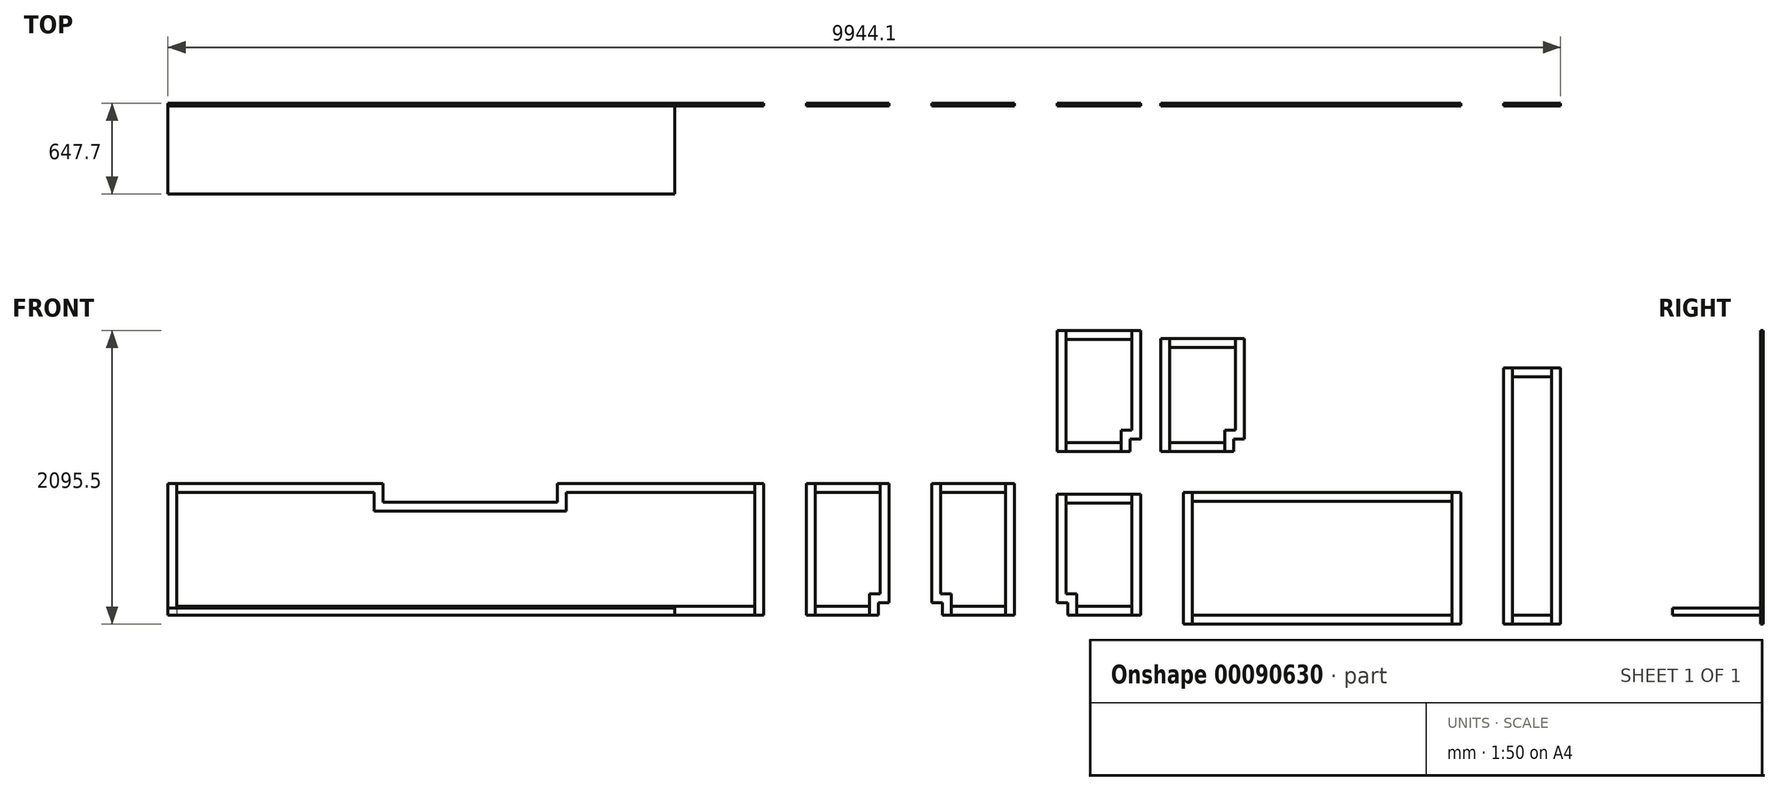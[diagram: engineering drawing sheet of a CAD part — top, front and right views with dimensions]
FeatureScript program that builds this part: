
annotation { "Feature Type Name" : "Feature", "Feature Type Description" : "" }
export const myFeature = defineFeature(function(context is Context, id is Id, definition is map)
    precondition{}
    {
        {
            var Q0;
            Q0=qCreatedBy(makeId("Top.planeOp"),FACE);
            var sketch = newSketch(context, id + "F0", { "sketchPlane" : qUnion([Q0])});
            skLineSegment(sketch, "E0.bottom", {"start": v(0, 0) * mm, "end": v(3619.5, 0) * mm});
            skLineSegment(sketch, "E0.top", {"start": v(0, -647.7) * mm, "end": v(3619.5, -647.7) * mm});
            skLineSegment(sketch, "E0.left", {"start": v(0, 0) * mm, "end": v(0, -647.7) * mm});
            skLineSegment(sketch, "E0.right", {"start": v(3619.5, 0) * mm, "end": v(3619.5, -647.7) * mm});
            skSolve(sketch);
        }
        {
            var Q0;
            Q0 = qSketchRegion(id + "F0", true);
            extrude(context, id + "F1", {"entities" : qUnion([Q0]), "depth" : 50.8 * mm});
        }
        {
            var Q0;
            Q0=qCreatedBy(makeId("Front.planeOp"),FACE);
            var sketch = newSketch(context, id + "F2", { "sketchPlane" : qUnion([Q0])});
            skLineSegment(sketch, "E1.bottom", {"start": v(0, 0) * mm, "end": v(4254.5, 0) * mm});
            skLineSegment(sketch, "E1.top", {"start": v(0, 939.8) * mm, "end": v(4254.5, 939.8) * mm});
            skLineSegment(sketch, "E1.left", {"start": v(0, 0) * mm, "end": v(0, 939.8) * mm});
            skLineSegment(sketch, "E1.right", {"start": v(4254.5, 0) * mm, "end": v(4254.5, 939.8) * mm});
            skLineSegment(sketch, "E2", {"start": v(1536.7, 939.8) * mm, "end": v(1536.7, 806.45) * mm});
            skLineSegment(sketch, "E3", {"start": v(1536.7, 806.45) * mm, "end": v(2781.3, 806.45) * mm});
            skLineSegment(sketch, "E4", {"start": v(2781.3, 806.45) * mm, "end": v(2781.3, 939.8) * mm});
            skLineSegment(sketch, "E5", {"start": v(63.5, 939.8) * mm, "end": v(63.5, 0) * mm});
            skLineSegment(sketch, "E6", {"start": v(4191, 939.8) * mm, "end": v(4191, 0) * mm});
            skLineSegment(sketch, "E7", {"start": v(63.5, 876.3) * mm, "end": v(1473.2, 876.3) * mm});
            skLineSegment(sketch, "E8", {"start": v(1473.2, 876.3) * mm, "end": v(1473.2, 742.95) * mm});
            skLineSegment(sketch, "E9", {"start": v(1473.2, 742.95) * mm, "end": v(2844.8, 742.95) * mm});
            skLineSegment(sketch, "E10", {"start": v(2844.8, 742.95) * mm, "end": v(2844.8, 876.3) * mm});
            skLineSegment(sketch, "E11", {"start": v(2844.8, 876.3) * mm, "end": v(4191, 876.3) * mm});
            skLineSegment(sketch, "E12", {"start": v(63.5, 63.5) * mm, "end": v(4191, 63.5) * mm});
            skLineSegment(sketch, "E13", {"start": v(4191, 469.9) * mm, "end": v(4254.5, 469.9) * mm, "construction": true});
            skLineSegment(sketch, "E14", {"start": v(3517.9, 876.3) * mm, "end": v(3517.9, 939.8) * mm, "construction": true});
            skLineSegment(sketch, "E15", {"start": v(2844.8, 876.3) * mm, "end": v(2781.3, 876.3) * mm, "construction": true});
            skLineSegment(sketch, "E16", {"start": v(2144.3, 806.45) * mm, "end": v(2144.3, 742.95) * mm, "construction": true});
            skLineSegment(sketch, "E17", {"start": v(1473.2, 824.4) * mm, "end": v(1536.7, 824.4) * mm, "construction": true});
            skLineSegment(sketch, "E18", {"start": v(768.35, 876.3) * mm, "end": v(768.35, 939.8) * mm, "construction": true});
            skLineSegment(sketch, "E19", {"start": v(63.5, 469.9) * mm, "end": v(0, 469.9) * mm, "construction": true});
            skLineSegment(sketch, "E20", {"start": v(1679.38, 63.5) * mm, "end": v(1679.38, 0) * mm, "construction": true});
            skSolve(sketch);
        }
        {
            var Q0;
            {var subQ4=sQuery(id+"F2.wireOp",EDGE,"E1.left");Q0=makeQuery(id+"F2.imprint","IMPRINT",FACE,{"disambiguationData":[TD([[makeQuery(id+"F2.imprint","IMPRINT",EDGE,{"derivedFrom":subQ4}),-1.0]])]});}
            var Q1;
            {var subQ0=sQuery(id+"F2.wireOp",EDGE,"E1.right");Q1=makeQuery(id+"F2.imprint","IMPRINT",FACE,{"disambiguationData":[TD([[makeQuery(id+"F2.imprint","IMPRINT",EDGE,{"derivedFrom":subQ0}),1.0]])]});}
            extrude(context, id + "F3", {"entities" : qUnion([Q0, Q1]), "depth" : 19.05 * mm});
        }
        {
            var Q0;
            {var subQ8=sQuery(id+"F2.wireOp",EDGE,"E2");Q0=makeQuery(id+"F2.imprint","IMPRINT",FACE,{"disambiguationData":[TD([[makeQuery(id+"F2.imprint","IMPRINT",EDGE,{"derivedFrom":subQ8}),-1.0]])]});}
            var Q1;
            {var subQ5=sQuery(id+"F2.wireOp",EDGE,"E12");Q1=makeQuery(id+"F2.imprint","IMPRINT",FACE,{"disambiguationData":[TD([[makeQuery(id+"F2.imprint","IMPRINT",EDGE,{"derivedFrom":subQ5}),-1.0]])]});}
            extrude(context, id + "F4", {"entities" : qUnion([Q0, Q1]), "depth" : 19.05 * mm});
        }
        {
            var Q0;
            {var subQ0=sQuery(id+"F2.wireOp",EDGE,"E7");Q0=makeQuery(id+"F2.imprint","IMPRINT",FACE,{"disambiguationData":[TD([[makeQuery(id+"F2.imprint","IMPRINT",EDGE,{"derivedFrom":subQ0}),-1.0]])]});}
            extrude(context, id + "F5", {"entities" : qUnion([Q0]), "depth" : 9.52 * mm});
        }
        {
            var Q0;
            Q0=qCreatedBy(makeId("Front.planeOp"),FACE);
            var sketch = newSketch(context, id + "F6", { "sketchPlane" : qUnion([Q0])});
            skLineSegment(sketch, "E21.bottom", {"start": v(4559.3, 0) * mm, "end": v(5149.85, 0) * mm});
            skLineSegment(sketch, "E21.top", {"start": v(4559.3, 939.8) * mm, "end": v(5149.85, 939.8) * mm});
            skLineSegment(sketch, "E21.left", {"start": v(4559.3, 0) * mm, "end": v(4559.3, 939.8) * mm});
            skLineSegment(sketch, "E21.right", {"start": v(5149.85, 0) * mm, "end": v(5149.85, 939.8) * mm});
            skLineSegment(sketch, "E22", {"start": v(5073.65, 0) * mm, "end": v(5073.65, 88.9) * mm});
            skLineSegment(sketch, "E23", {"start": v(5073.65, 88.9) * mm, "end": v(5149.85, 88.9) * mm});
            skLineSegment(sketch, "E24", {"start": v(4622.8, 939.8) * mm, "end": v(4622.8, 0) * mm});
            skLineSegment(sketch, "E25", {"start": v(5086.35, 939.8) * mm, "end": v(5086.35, 152.4) * mm});
            skLineSegment(sketch, "E26", {"start": v(5086.35, 152.4) * mm, "end": v(5010.15, 152.4) * mm});
            skLineSegment(sketch, "E27", {"start": v(5010.15, 152.4) * mm, "end": v(5010.15, 0) * mm});
            skLineSegment(sketch, "E28", {"start": v(4622.8, 63.5) * mm, "end": v(5010.15, 63.5) * mm});
            skLineSegment(sketch, "E29", {"start": v(4622.8, 876.3) * mm, "end": v(5086.35, 876.3) * mm});
            skLineSegment(sketch, "E30", {"start": v(4854.57, 939.8) * mm, "end": v(4854.57, 876.3) * mm, "construction": true});
            skLineSegment(sketch, "E31", {"start": v(5149.85, 469.9) * mm, "end": v(5086.35, 469.9) * mm, "construction": true});
            skLineSegment(sketch, "E32", {"start": v(4559.3, 469.9) * mm, "end": v(4622.8, 469.9) * mm, "construction": true});
            skLineSegment(sketch, "E33", {"start": v(4816.48, 63.5) * mm, "end": v(4816.48, 0) * mm, "construction": true});
            skLineSegment(sketch, "E34", {"start": v(5073.65, 44.45) * mm, "end": v(5010.15, 44.45) * mm, "construction": true});
            skLineSegment(sketch, "E35", {"start": v(5111.75, 88.9) * mm, "end": v(5111.75, 152.4) * mm, "construction": true});
            skLineSegment(sketch, "E36", {"start": v(5302.25, 0) * mm, "end": v(5302.25, 939.8) * mm, "construction": true});
            skLineSegment(sketch, "E37.MirrorCS", {"start": v(6045.2, 469.9) * mm, "end": v(5981.7, 469.9) * mm, "construction": true});
            skLineSegment(sketch, "E38.MirrorCS", {"start": v(5530.85, 44.45) * mm, "end": v(5594.35, 44.45) * mm, "construction": true});
            skLineSegment(sketch, "E39.MirrorCS", {"start": v(5749.93, 939.8) * mm, "end": v(5749.93, 876.3) * mm, "construction": true});
            skLineSegment(sketch, "E40.MirrorCS", {"start": v(5788.02, 63.5) * mm, "end": v(5788.02, 0) * mm, "construction": true});
            skLineSegment(sketch, "E41.MirrorCS", {"start": v(5454.65, 469.9) * mm, "end": v(5518.15, 469.9) * mm, "construction": true});
            skLineSegment(sketch, "E42.MirrorCS", {"start": v(5492.75, 88.9) * mm, "end": v(5492.75, 152.4) * mm, "construction": true});
            skLineSegment(sketch, "E43.MirrorCS", {"start": v(5530.85, 0) * mm, "end": v(5530.85, 88.9) * mm});
            skLineSegment(sketch, "E44.MirrorCS", {"start": v(5530.85, 88.9) * mm, "end": v(5454.65, 88.9) * mm});
            skLineSegment(sketch, "E45.MirrorCS", {"start": v(5594.35, 152.4) * mm, "end": v(5594.35, 0) * mm});
            skLineSegment(sketch, "E46.MirrorCS", {"start": v(5981.7, 63.5) * mm, "end": v(5594.35, 63.5) * mm});
            skLineSegment(sketch, "E47.MirrorCS", {"start": v(5518.15, 152.4) * mm, "end": v(5594.35, 152.4) * mm});
            skLineSegment(sketch, "E48.MirrorCS", {"start": v(5518.15, 939.8) * mm, "end": v(5518.15, 152.4) * mm});
            skLineSegment(sketch, "E49.MirrorCS", {"start": v(5981.7, 939.8) * mm, "end": v(5981.7, 0) * mm});
            skLineSegment(sketch, "E50.MirrorCS", {"start": v(6045.2, 0) * mm, "end": v(5454.65, 0) * mm});
            skLineSegment(sketch, "E51.MirrorCS", {"start": v(6045.2, 939.8) * mm, "end": v(5454.65, 939.8) * mm});
            skLineSegment(sketch, "E52.MirrorCS", {"start": v(6045.2, 0) * mm, "end": v(6045.2, 939.8) * mm});
            skLineSegment(sketch, "E53.MirrorCS", {"start": v(5454.65, 0) * mm, "end": v(5454.65, 939.8) * mm});
            skLineSegment(sketch, "E54.MirrorCS", {"start": v(5981.7, 876.3) * mm, "end": v(5518.15, 876.3) * mm});
            skLineSegment(sketch, "E55.bottom", {"start": v(6946.9, 0) * mm, "end": v(6350, 0) * mm});
            skLineSegment(sketch, "E55.top", {"start": v(6946.9, 863.6) * mm, "end": v(6350, 863.6) * mm});
            skLineSegment(sketch, "E55.left", {"start": v(6946.9, 0) * mm, "end": v(6946.9, 863.6) * mm});
            skLineSegment(sketch, "E55.right", {"start": v(6350, 0) * mm, "end": v(6350, 863.6) * mm});
            skLineSegment(sketch, "E56", {"start": v(6350, 88.9) * mm, "end": v(6426.2, 88.9) * mm});
            skLineSegment(sketch, "E57", {"start": v(6426.2, 88.9) * mm, "end": v(6426.2, 0) * mm});
            skLineSegment(sketch, "E58", {"start": v(6413.5, 863.6) * mm, "end": v(6413.5, 152.4) * mm});
            skLineSegment(sketch, "E59", {"start": v(6413.5, 152.4) * mm, "end": v(6489.7, 152.4) * mm});
            skLineSegment(sketch, "E60", {"start": v(6489.7, 152.4) * mm, "end": v(6489.7, 0) * mm});
            skLineSegment(sketch, "E61", {"start": v(6883.4, 0) * mm, "end": v(6883.4, 863.6) * mm});
            skLineSegment(sketch, "E62", {"start": v(6883.4, 800.1) * mm, "end": v(6413.5, 800.1) * mm});
            skLineSegment(sketch, "E63", {"start": v(6489.7, 63.5) * mm, "end": v(6883.4, 63.5) * mm});
            skLineSegment(sketch, "E64", {"start": v(6946.9, 431.8) * mm, "end": v(6883.4, 431.8) * mm, "construction": true});
            skLineSegment(sketch, "E65", {"start": v(6648.45, 863.6) * mm, "end": v(6648.45, 800.1) * mm, "construction": true});
            skLineSegment(sketch, "E66", {"start": v(6350, 431.8) * mm, "end": v(6413.5, 431.8) * mm, "construction": true});
            skLineSegment(sketch, "E67", {"start": v(6686.55, 63.5) * mm, "end": v(6686.55, 0) * mm, "construction": true});
            skLineSegment(sketch, "E68", {"start": v(6426.2, 44.45) * mm, "end": v(6489.7, 44.45) * mm, "construction": true});
            skLineSegment(sketch, "E69", {"start": v(6388.1, 88.9) * mm, "end": v(6388.1, 152.4) * mm, "construction": true});
            skLineSegment(sketch, "E70.bottom", {"start": v(7251.7, 876.3) * mm, "end": v(9232.9, 876.3) * mm});
            skLineSegment(sketch, "E70.top", {"start": v(7251.7, -63.5) * mm, "end": v(9232.9, -63.5) * mm});
            skLineSegment(sketch, "E70.left", {"start": v(7251.7, 876.3) * mm, "end": v(7251.7, -63.5) * mm});
            skLineSegment(sketch, "E70.right", {"start": v(9232.9, 876.3) * mm, "end": v(9232.9, -63.5) * mm});
            skLineSegment(sketch, "E71", {"start": v(7315.2, 876.3) * mm, "end": v(7315.2, -63.5) * mm});
            skLineSegment(sketch, "E72", {"start": v(9169.4, 876.3) * mm, "end": v(9169.4, -63.5) * mm});
            skLineSegment(sketch, "E73", {"start": v(7315.2, 812.8) * mm, "end": v(9169.4, 812.8) * mm});
            skLineSegment(sketch, "E74", {"start": v(7315.2, 0) * mm, "end": v(9169.4, 0) * mm});
            skLineSegment(sketch, "E75", {"start": v(9232.9, 406.4) * mm, "end": v(9169.4, 406.4) * mm, "construction": true});
            skLineSegment(sketch, "E76", {"start": v(8261.12, 876.3) * mm, "end": v(8261.12, 812.8) * mm, "construction": true});
            skLineSegment(sketch, "E77", {"start": v(7251.7, 406.4) * mm, "end": v(7315.2, 406.4) * mm, "construction": true});
            skLineSegment(sketch, "E78", {"start": v(8242.3, 0) * mm, "end": v(8242.3, -63.5) * mm, "construction": true});
            skLineSegment(sketch, "E79.bottom", {"start": v(9537.7, -63.5) * mm, "end": v(9944.1, -63.5) * mm});
            skLineSegment(sketch, "E79.top", {"start": v(9537.7, 1765.3) * mm, "end": v(9944.1, 1765.3) * mm});
            skLineSegment(sketch, "E79.left", {"start": v(9537.7, -63.5) * mm, "end": v(9537.7, 1765.3) * mm});
            skLineSegment(sketch, "E79.right", {"start": v(9944.1, -63.5) * mm, "end": v(9944.1, 1765.3) * mm});
            skLineSegment(sketch, "E80.bottom", {"start": v(9880.6, 0) * mm, "end": v(9601.2, 0) * mm});
            skLineSegment(sketch, "E80.top", {"start": v(9880.6, 1701.8) * mm, "end": v(9601.2, 1701.8) * mm});
            skLineSegment(sketch, "E80.left", {"start": v(9880.6, 0) * mm, "end": v(9880.6, 1701.8) * mm});
            skLineSegment(sketch, "E80.right", {"start": v(9601.2, 0) * mm, "end": v(9601.2, 1701.8) * mm});
            skLineSegment(sketch, "E81", {"start": v(9740.9, 1765.3) * mm, "end": v(9740.9, 1701.8) * mm, "construction": true});
            skPoint(sketch, "E81.endSnap0", {"position": v(9740.9, 1701.8) * mm});
            skLineSegment(sketch, "E82", {"start": v(9944.1, 850.9) * mm, "end": v(9880.6, 850.9) * mm, "construction": true});
            skLineSegment(sketch, "E83", {"start": v(9537.7, 850.9) * mm, "end": v(9601.2, 850.9) * mm, "construction": true});
            skLineSegment(sketch, "E84", {"start": v(9740.9, -63.5) * mm, "end": v(9740.9, 0) * mm, "construction": true});
            skLineSegment(sketch, "E85", {"start": v(9601.2, 1701.8) * mm, "end": v(9601.2, 1765.3) * mm});
            skLineSegment(sketch, "E86", {"start": v(9880.6, 1701.8) * mm, "end": v(9880.6, 1765.3) * mm});
            skLineSegment(sketch, "E87", {"start": v(9601.2, 0) * mm, "end": v(9601.2, -63.5) * mm});
            skLineSegment(sketch, "E88", {"start": v(9880.6, 0) * mm, "end": v(9880.6, -63.5) * mm});
            skLineSegment(sketch, "E89.bottom", {"start": v(6350, 2032) * mm, "end": v(6946.9, 2032) * mm});
            skLineSegment(sketch, "E89.top", {"start": v(6350, 1168.4) * mm, "end": v(6946.9, 1168.4) * mm});
            skLineSegment(sketch, "E89.left", {"start": v(6350, 2032) * mm, "end": v(6350, 1168.4) * mm});
            skLineSegment(sketch, "E89.right", {"start": v(6946.9, 2032) * mm, "end": v(6946.9, 1168.4) * mm});
            skLineSegment(sketch, "E90", {"start": v(6883.4, 2032) * mm, "end": v(6883.4, 1320.8) * mm});
            skLineSegment(sketch, "E91", {"start": v(6883.4, 1320.8) * mm, "end": v(6807.2, 1320.8) * mm});
            skLineSegment(sketch, "E92", {"start": v(6807.2, 1320.8) * mm, "end": v(6807.2, 1168.4) * mm});
            skLineSegment(sketch, "E93", {"start": v(6413.5, 2032) * mm, "end": v(6413.5, 1168.4) * mm});
            skLineSegment(sketch, "E94", {"start": v(6413.5, 1968.5) * mm, "end": v(6883.4, 1968.5) * mm});
            skLineSegment(sketch, "E95", {"start": v(6807.2, 1231.9) * mm, "end": v(6413.5, 1231.9) * mm});
            skLineSegment(sketch, "E96", {"start": v(6610.35, 1231.9) * mm, "end": v(6610.35, 1168.4) * mm, "construction": true});
            skLineSegment(sketch, "E97", {"start": v(6413.5, 1600.2) * mm, "end": v(6350, 1600.2) * mm, "construction": true});
            skLineSegment(sketch, "E98", {"start": v(6883.4, 1676.4) * mm, "end": v(6946.9, 1676.4) * mm, "construction": true});
            skLineSegment(sketch, "E99", {"start": v(6648.45, 1968.5) * mm, "end": v(6648.45, 2032) * mm, "construction": true});
            skLineSegment(sketch, "E100", {"start": v(6870.7, 1168.4) * mm, "end": v(6870.7, 1257.3) * mm});
            skLineSegment(sketch, "E101", {"start": v(6870.7, 1257.3) * mm, "end": v(6946.9, 1257.3) * mm});
            skLineSegment(sketch, "E102.bottom", {"start": v(7089.73, 1974.85) * mm, "end": v(7686.63, 1974.85) * mm});
            skLineSegment(sketch, "E102.top", {"start": v(7089.73, 1168.4) * mm, "end": v(7686.63, 1168.4) * mm});
            skLineSegment(sketch, "E102.left", {"start": v(7089.73, 1974.85) * mm, "end": v(7089.73, 1168.4) * mm});
            skLineSegment(sketch, "E102.right", {"start": v(7686.63, 1974.85) * mm, "end": v(7686.63, 1168.4) * mm});
            skLineSegment(sketch, "E103", {"start": v(7623.13, 1974.85) * mm, "end": v(7623.13, 1320.8) * mm});
            skLineSegment(sketch, "E104", {"start": v(7623.13, 1320.8) * mm, "end": v(7546.93, 1320.8) * mm});
            skLineSegment(sketch, "E105", {"start": v(7546.93, 1320.8) * mm, "end": v(7546.93, 1168.4) * mm});
            skLineSegment(sketch, "E106", {"start": v(7153.23, 1974.85) * mm, "end": v(7153.23, 1168.4) * mm});
            skLineSegment(sketch, "E107", {"start": v(7153.23, 1911.35) * mm, "end": v(7623.13, 1911.35) * mm});
            skLineSegment(sketch, "E108", {"start": v(7546.93, 1231.9) * mm, "end": v(7153.23, 1231.9) * mm});
            skLineSegment(sketch, "E109", {"start": v(7350.08, 1231.9) * mm, "end": v(7350.08, 1168.4) * mm, "construction": true});
            skLineSegment(sketch, "E110", {"start": v(7153.23, 1571.62) * mm, "end": v(7089.73, 1571.62) * mm, "construction": true});
            skLineSegment(sketch, "E111", {"start": v(7623.13, 1647.83) * mm, "end": v(7686.63, 1647.83) * mm, "construction": true});
            skLineSegment(sketch, "E112", {"start": v(7388.18, 1911.35) * mm, "end": v(7388.18, 1974.85) * mm, "construction": true});
            skLineSegment(sketch, "E113", {"start": v(7610.43, 1168.4) * mm, "end": v(7610.43, 1257.3) * mm});
            skLineSegment(sketch, "E114", {"start": v(7610.43, 1257.3) * mm, "end": v(7686.63, 1257.3) * mm});
            skSolve(sketch);
        }
        {
            var Q0;
            {var subQ0=sQuery(id+"F6.wireOp",EDGE,"E21.left");Q0=makeQuery(id+"F6.imprint","IMPRINT",FACE,{"disambiguationData":[TD([[makeQuery(id+"F6.imprint","IMPRINT",EDGE,{"derivedFrom":subQ0}),-1.0]])]});}
            var Q1;
            {var subQ4=sQuery(id+"F6.wireOp",EDGE,"E22");Q1=makeQuery(id+"F6.imprint","IMPRINT",FACE,{"disambiguationData":[TD([[makeQuery(id+"F6.imprint","IMPRINT",EDGE,{"derivedFrom":subQ4}),1.0]])]});}
            var Q2;
            {var subQ4=sQuery(id+"F6.wireOp",EDGE,"E43.MirrorCS");Q2=makeQuery(id+"F6.imprint","IMPRINT",FACE,{"disambiguationData":[TD([[makeQuery(id+"F6.imprint","IMPRINT",EDGE,{"derivedFrom":subQ4}),-1.0]])]});}
            var Q3;
            {var subQ3=sQuery(id+"F6.wireOp",EDGE,"E52.MirrorCS");Q3=makeQuery(id+"F6.imprint","IMPRINT",FACE,{"disambiguationData":[TD([[makeQuery(id+"F6.imprint","IMPRINT",EDGE,{"derivedFrom":subQ3}),1.0]])]});}
            var Q4;
            {var subQ3=sQuery(id+"F6.wireOp",EDGE,"E56");Q4=makeQuery(id+"F6.imprint","IMPRINT",FACE,{"disambiguationData":[TD([[makeQuery(id+"F6.imprint","IMPRINT",EDGE,{"derivedFrom":subQ3}),1.0]])]});}
            var Q5;
            {var subQ4=sQuery(id+"F6.wireOp",EDGE,"E55.left");Q5=makeQuery(id+"F6.imprint","IMPRINT",FACE,{"disambiguationData":[TD([[makeQuery(id+"F6.imprint","IMPRINT",EDGE,{"derivedFrom":subQ4}),1.0]])]});}
            var Q6;
            {var subQ0=sQuery(id+"F6.wireOp",EDGE,"E70.left");Q6=makeQuery(id+"F6.imprint","IMPRINT",FACE,{"disambiguationData":[TD([[makeQuery(id+"F6.imprint","IMPRINT",EDGE,{"derivedFrom":subQ0}),1.0]])]});}
            var Q7;
            {var subQ4=sQuery(id+"F6.wireOp",EDGE,"E70.right");Q7=makeQuery(id+"F6.imprint","IMPRINT",FACE,{"disambiguationData":[TD([[makeQuery(id+"F6.imprint","IMPRINT",EDGE,{"derivedFrom":subQ4}),-1.0]])]});}
            extrude(context, id + "F7", {"entities" : qUnion([Q0, Q1, Q2, Q3, Q4, Q5, Q6, Q7]), "depth" : 19.05 * mm});
        }
        {
            var Q0;
            {var subQ5=sQuery(id+"F6.wireOp",EDGE,"E29");Q0=makeQuery(id+"F6.imprint","IMPRINT",FACE,{"disambiguationData":[TD([[makeQuery(id+"F6.imprint","IMPRINT",EDGE,{"derivedFrom":subQ5}),1.0]])]});}
            var Q1;
            {var subQ5=sQuery(id+"F6.wireOp",EDGE,"E28");Q1=makeQuery(id+"F6.imprint","IMPRINT",FACE,{"disambiguationData":[TD([[makeQuery(id+"F6.imprint","IMPRINT",EDGE,{"derivedFrom":subQ5}),-1.0]])]});}
            var Q2;
            {var subQ3=sQuery(id+"F6.wireOp",EDGE,"E54.MirrorCS");Q2=makeQuery(id+"F6.imprint","IMPRINT",FACE,{"disambiguationData":[TD([[makeQuery(id+"F6.imprint","IMPRINT",EDGE,{"derivedFrom":subQ3}),-1.0]])]});}
            var Q3;
            {var subQ3=sQuery(id+"F6.wireOp",EDGE,"E46.MirrorCS");Q3=makeQuery(id+"F6.imprint","IMPRINT",FACE,{"disambiguationData":[TD([[makeQuery(id+"F6.imprint","IMPRINT",EDGE,{"derivedFrom":subQ3}),1.0]])]});}
            var Q4;
            {var subQ5=sQuery(id+"F6.wireOp",EDGE,"E62");Q4=makeQuery(id+"F6.imprint","IMPRINT",FACE,{"disambiguationData":[TD([[makeQuery(id+"F6.imprint","IMPRINT",EDGE,{"derivedFrom":subQ5}),-1.0]])]});}
            var Q5;
            {var subQ5=sQuery(id+"F6.wireOp",EDGE,"E63");Q5=makeQuery(id+"F6.imprint","IMPRINT",FACE,{"disambiguationData":[TD([[makeQuery(id+"F6.imprint","IMPRINT",EDGE,{"derivedFrom":subQ5}),-1.0]])]});}
            var Q6;
            {var subQ5=sQuery(id+"F6.wireOp",EDGE,"E73");Q6=makeQuery(id+"F6.imprint","IMPRINT",FACE,{"disambiguationData":[TD([[makeQuery(id+"F6.imprint","IMPRINT",EDGE,{"derivedFrom":subQ5}),1.0]])]});}
            var Q7;
            {var subQ5=sQuery(id+"F6.wireOp",EDGE,"E74");Q7=makeQuery(id+"F6.imprint","IMPRINT",FACE,{"disambiguationData":[TD([[makeQuery(id+"F6.imprint","IMPRINT",EDGE,{"derivedFrom":subQ5}),-1.0]])]});}
            extrude(context, id + "F8", {"entities" : qUnion([Q0, Q1, Q2, Q3, Q4, Q5, Q6, Q7]), "depth" : 19.05 * mm});
        }
        {
            var Q0;
            {var subQ0=sQuery(id+"F6.wireOp",EDGE,"E73");Q0=makeQuery(id+"F6.imprint","IMPRINT",FACE,{"disambiguationData":[TD([[makeQuery(id+"F6.imprint","IMPRINT",EDGE,{"derivedFrom":subQ0}),-1.0]])]});}
            var Q1;
            {var subQ3=sQuery(id+"F6.wireOp",EDGE,"E59");Q1=makeQuery(id+"F6.imprint","IMPRINT",FACE,{"disambiguationData":[TD([[makeQuery(id+"F6.imprint","IMPRINT",EDGE,{"derivedFrom":subQ3}),1.0]])]});}
            var Q2;
            {var subQ3=sQuery(id+"F6.wireOp",EDGE,"E46.MirrorCS");Q2=makeQuery(id+"F6.imprint","IMPRINT",FACE,{"disambiguationData":[TD([[makeQuery(id+"F6.imprint","IMPRINT",EDGE,{"derivedFrom":subQ3}),-1.0]])]});}
            var Q3;
            {var subQ0=sQuery(id+"F6.wireOp",EDGE,"E26");Q3=makeQuery(id+"F6.imprint","IMPRINT",FACE,{"disambiguationData":[TD([[makeQuery(id+"F6.imprint","IMPRINT",EDGE,{"derivedFrom":subQ0}),-1.0]])]});}
            extrude(context, id + "F9", {"entities" : qUnion([Q0, Q1, Q2, Q3]), "depth" : 9.52 * mm});
        }
        {
            var Q0;
            {var subQ1=sQuery(id+"F6.wireOp",EDGE,"E79.left");Q0=makeQuery(id+"F6.imprint","IMPRINT",FACE,{"disambiguationData":[TD([[makeQuery(id+"F6.imprint","IMPRINT",EDGE,{"derivedFrom":subQ1}),-1.0]])]});}
            var Q1;
            {var subQ1=sQuery(id+"F6.wireOp",EDGE,"E79.right");Q1=makeQuery(id+"F6.imprint","IMPRINT",FACE,{"disambiguationData":[TD([[makeQuery(id+"F6.imprint","IMPRINT",EDGE,{"derivedFrom":subQ1}),1.0]])]});}
            extrude(context, id + "F10", {"entities" : qUnion([Q0, Q1]), "depth" : 19.05 * mm});
        }
        {
            var Q0;
            Q0=makeQuery(id+"F6.imprint","IMPRINT",FACE,{"disambiguationData":[TD([[makeQuery(id+"F6.imprint","IMPRINT",EDGE,{"derivedFrom":sQuery(id+"F6.wireOp",EDGE,"E80.bottom")}),1.0]])]});
            var Q1;
            Q1=makeQuery(id+"F6.imprint","IMPRINT",FACE,{"disambiguationData":[TD([[makeQuery(id+"F6.imprint","IMPRINT",EDGE,{"derivedFrom":sQuery(id+"F6.wireOp",EDGE,"E80.top")}),-1.0]])]});
            var Q2;
            Q2=makeQuery(id+"F10.opExtrude","CAP_FACE",FACE,{"disambiguationData":[OSD([sQuery(id+"F6.wireOp",EDGE,"E79.bottom"),sQuery(id+"F6.wireOp",EDGE,"E79.top"),sQuery(id+"F6.wireOp",EDGE,"E79.right"),sQuery(id+"F6.wireOp",EDGE,"E80.left"),sQuery(id+"F6.wireOp",EDGE,"E86"),sQuery(id+"F6.wireOp",EDGE,"E88")])],"isStart":false});
            extrude(context, id + "F11", {"entities" : qUnion([Q0, Q1]), "endBound" : BoundingType.UP_TO_SURFACE, "endBoundEntityFace" : qUnion([Q2]), "depth" : 25.4 * mm});
        }
        {
            var Q0;
            Q0=makeQuery(id+"F6.imprint","IMPRINT",FACE,{"disambiguationData":[TD([[makeQuery(id+"F6.imprint","IMPRINT",EDGE,{"derivedFrom":sQuery(id+"F6.wireOp",EDGE,"E80.bottom")}),-1.0]])]});
            extrude(context, id + "F12", {"entities" : qUnion([Q0]), "depth" : 9.52 * mm});
        }
        {
            var Q0;
            {var subQ4=sQuery(id+"F6.wireOp",EDGE,"E89.left");Q0=makeQuery(id+"F6.imprint","IMPRINT",FACE,{"disambiguationData":[TD([[makeQuery(id+"F6.imprint","IMPRINT",EDGE,{"derivedFrom":subQ4}),1.0]])]});}
            var Q1;
            {var subQ11=sQuery(id+"F6.wireOp",EDGE,"E91");Q1=makeQuery(id+"F6.imprint","IMPRINT",FACE,{"disambiguationData":[TD([[makeQuery(id+"F6.imprint","IMPRINT",EDGE,{"derivedFrom":subQ11}),1.0]])]});}
            extrude(context, id + "F13", {"entities" : qUnion([Q0, Q1]), "depth" : 19.05 * mm});
        }
        {
            var Q0;
            {var subQ5=sQuery(id+"F6.wireOp",EDGE,"E94");Q0=makeQuery(id+"F6.imprint","IMPRINT",FACE,{"disambiguationData":[TD([[makeQuery(id+"F6.imprint","IMPRINT",EDGE,{"derivedFrom":subQ5}),1.0]])]});}
            var Q1;
            {var subQ5=sQuery(id+"F6.wireOp",EDGE,"E95");Q1=makeQuery(id+"F6.imprint","IMPRINT",FACE,{"disambiguationData":[TD([[makeQuery(id+"F6.imprint","IMPRINT",EDGE,{"derivedFrom":subQ5}),1.0]])]});}
            extrude(context, id + "F14", {"entities" : qUnion([Q0, Q1]), "depth" : 19.05 * mm});
        }
        {
            var Q0;
            {var subQ4=sQuery(id+"F6.wireOp",EDGE,"E91");Q0=makeQuery(id+"F6.imprint","IMPRINT",FACE,{"disambiguationData":[TD([[makeQuery(id+"F6.imprint","IMPRINT",EDGE,{"derivedFrom":subQ4}),-1.0]])]});}
            extrude(context, id + "F15", {"entities" : qUnion([Q0]), "depth" : 9.52 * mm});
        }
        {
            var Q0;
            {var subQ4=sQuery(id+"F6.wireOp",EDGE,"E102.left");Q0=makeQuery(id+"F6.imprint","IMPRINT",FACE,{"disambiguationData":[TD([[makeQuery(id+"F6.imprint","IMPRINT",EDGE,{"derivedFrom":subQ4}),1.0]])]});}
            var Q1;
            {var subQ11=sQuery(id+"F6.wireOp",EDGE,"E104");Q1=makeQuery(id+"F6.imprint","IMPRINT",FACE,{"disambiguationData":[TD([[makeQuery(id+"F6.imprint","IMPRINT",EDGE,{"derivedFrom":subQ11}),1.0]])]});}
            extrude(context, id + "F16", {"entities" : qUnion([Q0, Q1]), "depth" : 19.05 * mm});
        }
        {
            var Q0;
            {var subQ5=sQuery(id+"F6.wireOp",EDGE,"E107");Q0=makeQuery(id+"F6.imprint","IMPRINT",FACE,{"disambiguationData":[TD([[makeQuery(id+"F6.imprint","IMPRINT",EDGE,{"derivedFrom":subQ5}),1.0]])]});}
            var Q1;
            {var subQ5=sQuery(id+"F6.wireOp",EDGE,"E108");Q1=makeQuery(id+"F6.imprint","IMPRINT",FACE,{"disambiguationData":[TD([[makeQuery(id+"F6.imprint","IMPRINT",EDGE,{"derivedFrom":subQ5}),1.0]])]});}
            extrude(context, id + "F17", {"entities" : qUnion([Q0, Q1]), "depth" : 19.05 * mm});
        }
        {
            var Q0;
            {var subQ4=sQuery(id+"F6.wireOp",EDGE,"E104");Q0=makeQuery(id+"F6.imprint","IMPRINT",FACE,{"disambiguationData":[TD([[makeQuery(id+"F6.imprint","IMPRINT",EDGE,{"derivedFrom":subQ4}),-1.0]])]});}
            extrude(context, id + "F18", {"entities" : qUnion([Q0]), "depth" : 9.52 * mm});
        }
    });
